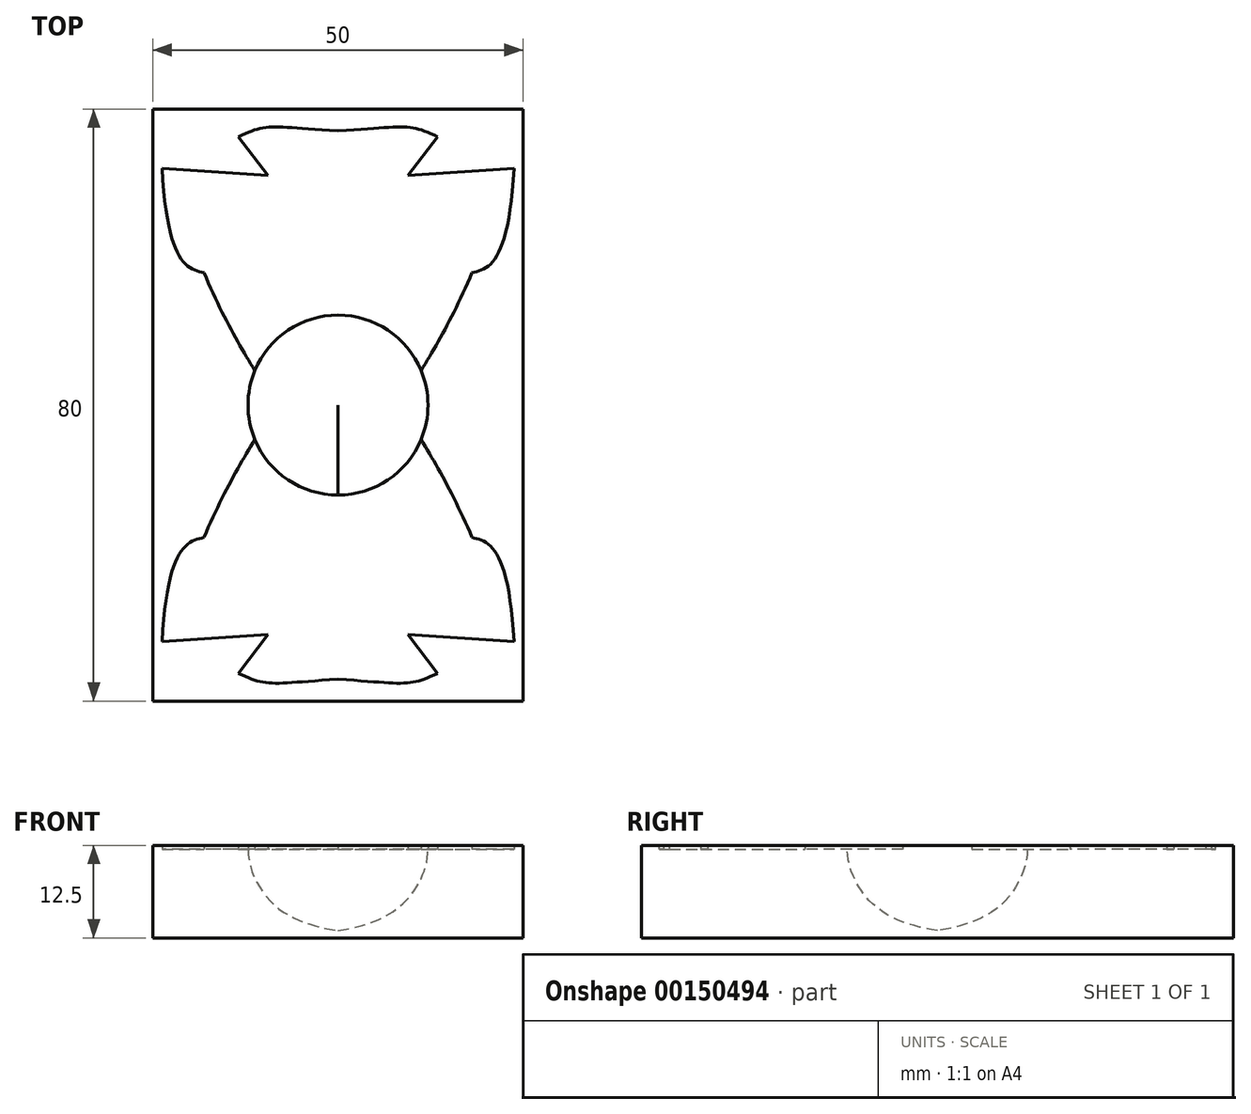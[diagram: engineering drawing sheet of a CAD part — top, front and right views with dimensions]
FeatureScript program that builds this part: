
annotation { "Feature Type Name" : "Feature", "Feature Type Description" : "" }
export const myFeature = defineFeature(function(context is Context, id is Id, definition is map)
    precondition{}
    {
        {
            var Q0;
            Q0=qCreatedBy(makeId("Top.planeOp"),FACE);
            var sketch = newSketch(context, id + "F0", { "sketchPlane" : qUnion([Q0])});
            skLineSegment(sketch, "E0.bottom", {"start": v(-60.64, -67.64) * mm, "end": v(-10.64, -67.64) * mm});
            skLineSegment(sketch, "E0.top", {"start": v(-60.64, -147.64) * mm, "end": v(-10.64, -147.64) * mm});
            skLineSegment(sketch, "E0.left", {"start": v(-60.64, -67.64) * mm, "end": v(-60.64, -147.64) * mm});
            skLineSegment(sketch, "E0.right", {"start": v(-10.64, -67.64) * mm, "end": v(-10.64, -147.64) * mm});
            skSolve(sketch);
        }
        {
            var Q0;
            Q0=makeQuery(id+"F0.imprint","IMPRINT",FACE,{"disambiguationData":[TD([[makeQuery(id+"F0.imprint","IMPRINT",EDGE,{"derivedFrom":sQuery(id+"F0.wireOp",EDGE,"E0.bottom")}),-1.0]])]});
            extrude(context, id + "F1", {"entities" : qUnion([Q0]), "depth" : 12 * mm});
        }
        {
            var Q0;
            Q0=makeQuery(id+"F1.opExtrude","SWEPT_FACE",FACE,{"disambiguationData":[OSD([sQuery(id+"F0.wireOp",EDGE,"E0.right")])]});
            cPlane(context, id + "F2", {"entities" : qUnion([Q0]), "cplaneType" : CPlaneType.OFFSET, "offset" : 25 * mm, "oppositeDirection" : true, "width" : 150 * mm, "height" : 150 * mm});
        }
        {
            var Q0;
            Q0=qCreatedBy(id+"F2.planeOp",FACE);
            var sketch = newSketch(context, id + "F3", { "sketchPlane" : qUnion([Q0])});
            skFitSpline(sketch, "E1", {"points": [v(-107.63, 0.98) * mm, v(-116.16, 4.39) * mm, v(-119.8, 11.95) * mm, v(-116.72, 18.21) * mm, v(-107.63, 21) * mm], "startDerivative": vector(-36.59, 5.94) * mm, "endDerivative": vector(38.78, 5.13) * mm});
            skArc(sketch, "E2.trimOffspring", {"start": v(-107.64, 0.98) * mm, "mid": v(-107.64, 0.98) * mm, "end": v(-107.63, 0.98) * mm});
            skLineSegment(sketch, "E3", {"start": v(-107.64, 28.47) * mm, "end": v(-107.64, -7.44) * mm});
            skSolve(sketch);
        }
        {
            var Q0;
            {var subQ0=sQuery(id+"F3.wireOp",EDGE,"E1");Q0=makeQuery(id+"F3.imprint","IMPRINT",FACE,{"disambiguationData":[TD([[makeQuery(id+"F3.imprint","IMPRINT",EDGE,{"derivedFrom":subQ0}),-1.0]])]});}
            var Q1;
            Q1=sQuery(id+"F3.wireOp",EDGE,"E3");
            revolve(context, id + "F4", {"operationType" : NewBodyOperationType.REMOVE, "entities" : qUnion([Q0]), "axis" : qUnion([Q1]), "revolveType" : RevolveType.FULL, "oppositeDirection" : true});
        }
        {
            var Q0;
            Q0=makeQuery(id+"F1.opExtrude","CAP_FACE",FACE,{"disambiguationData":[OSD([sQuery(id+"F0.wireOp",EDGE,"E0.bottom"),sQuery(id+"F0.wireOp",EDGE,"E0.top"),sQuery(id+"F0.wireOp",EDGE,"E0.left"),sQuery(id+"F0.wireOp",EDGE,"E0.right")])],"isStart":false});
            var sketch = newSketch(context, id + "F5", { "sketchPlane" : qUnion([Q0])});
            skPoint(sketch, "E4.3.internal.snap0", {"position": v(-24.7, -91.33) * mm});
            skLineSegment(sketch, "E5.MirrorCS", {"start": v(-49.1, -71.4) * mm, "end": v(-45.08, -76.62) * mm});
            skLineSegment(sketch, "E6.MirrorCS", {"start": v(-45.08, -76.62) * mm, "end": v(-59.42, -75.67) * mm});
            skFitSpline(sketch, "E7.MirrorCS", {"points": [v(-35.64, -70.6) * mm, v(-49.1, -71.4) * mm], "startDerivative": vector(-27, 1.87) * mm, "endDerivative": vector(-11.52, -5.64) * mm});
            skFitSpline(sketch, "E8", {"points": [v(-59.42, -75.67) * mm, v(-53.45, -89.8) * mm, v(-48.56, -91.27) * mm, v(-40.85, -98.96) * mm, v(-58.03, -137.94) * mm], "startDerivative": vector(9.18, -160) * mm, "endDerivative": vector(-51.19, -186.4) * mm});
            skPoint(sketch, "E9.end.orphan", {"position": v(-10.64, -89.12) * mm});
            skLineSegment(sketch, "E10.bottom", {"start": v(-60.64, -67.64) * mm, "end": v(-10.64, -67.64) * mm});
            skLineSegment(sketch, "E10.top", {"start": v(-60.64, -147.64) * mm, "end": v(-10.64, -147.64) * mm});
            skLineSegment(sketch, "E10.left", {"start": v(-60.64, -67.64) * mm, "end": v(-60.64, -147.64) * mm});
            skLineSegment(sketch, "E10.right", {"start": v(-10.64, -67.64) * mm, "end": v(-10.64, -147.64) * mm});
            skLineSegment(sketch, "E11", {"start": v(-35.64, -107.64) * mm, "end": v(-47.8, -107.64) * mm});
            skLineSegment(sketch, "E12", {"start": v(-35.64, -107.64) * mm, "end": v(-35.64, -95.47) * mm});
            skPoint(sketch, "E4.0.internal.orphan", {"position": v(-12.1, -75.88) * mm});
            skPoint(sketch, "E4.2.internal.orphan", {"position": v(-24.7, -91.49) * mm});
            skPoint(sketch, "E4.4.internal.orphan", {"position": v(-12.1, -137.5) * mm});
            skFitSpline(sketch, "E13.MirrorCS", {"points": [v(-35.64, -70.6) * mm, v(-22.17, -71.4) * mm], "startDerivative": vector(27, 1.87) * mm, "endDerivative": vector(11.52, -5.64) * mm});
            skLineSegment(sketch, "E14.MirrorCS", {"start": v(-22.17, -71.4) * mm, "end": v(-26.2, -76.62) * mm});
            skLineSegment(sketch, "E15.MirrorCS", {"start": v(-26.2, -76.62) * mm, "end": v(-11.86, -75.67) * mm});
            skFitSpline(sketch, "E16.MirrorCS", {"points": [v(-11.86, -75.67) * mm, v(-17.83, -89.8) * mm, v(-22.72, -91.27) * mm, v(-30.43, -98.96) * mm, v(-13.25, -137.94) * mm], "startDerivative": vector(-9.18, -160) * mm, "endDerivative": vector(51.19, -186.4) * mm});
            skPoint(sketch, "E17.orphan", {"position": v(-42.15, -97.36) * mm});
            skPoint(sketch, "E18.MirrorCS.end.orphan", {"position": v(-29.13, -97.36) * mm});
            skPoint(sketch, "E18.MirrorCS.start.orphan", {"position": v(-29.63, -97.06) * mm});
            skCircle(sketch, "E19", {"center": v(-35.64, -107.64) * mm, "radius": 12.16 * mm});
            skFitSpline(sketch, "E20.MirrorCS", {"points": [v(-59.42, -139.6) * mm, v(-53.45, -125.47) * mm, v(-48.56, -124) * mm, v(-40.85, -116.31) * mm, v(-58.03, -77.33) * mm], "startDerivative": vector(9.18, 160) * mm, "endDerivative": vector(-51.19, 186.4) * mm});
            skLineSegment(sketch, "E21.MirrorCS", {"start": v(-45.08, -138.65) * mm, "end": v(-59.42, -139.6) * mm});
            skLineSegment(sketch, "E22.MirrorCS", {"start": v(-49.1, -143.88) * mm, "end": v(-45.08, -138.65) * mm});
            skFitSpline(sketch, "E23.MirrorCS", {"points": [v(-35.64, -144.67) * mm, v(-49.1, -143.88) * mm], "startDerivative": vector(-27, -1.87) * mm, "endDerivative": vector(-11.52, 5.64) * mm});
            skFitSpline(sketch, "E24.MirrorCS", {"points": [v(-35.64, -144.67) * mm, v(-22.17, -143.88) * mm], "startDerivative": vector(27, -1.87) * mm, "endDerivative": vector(11.52, 5.64) * mm});
            skLineSegment(sketch, "E25.MirrorCS", {"start": v(-22.17, -143.88) * mm, "end": v(-26.2, -138.65) * mm});
            skLineSegment(sketch, "E26.MirrorCS", {"start": v(-26.2, -138.65) * mm, "end": v(-11.86, -139.6) * mm});
            skFitSpline(sketch, "E27.MirrorCS", {"points": [v(-11.86, -139.6) * mm, v(-17.83, -125.47) * mm, v(-22.72, -124) * mm, v(-30.43, -116.31) * mm, v(-13.25, -77.33) * mm], "startDerivative": vector(-9.18, 160) * mm, "endDerivative": vector(51.19, 186.4) * mm});
            skSolve(sketch);
        }
        {
            var Q0;
            Q0=makeQuery(id+"F5.imprint","IMPRINT",FACE,{"disambiguationData":[TD([[makeQuery(id+"F5.imprint","IMPRINT",EDGE,{"derivedFrom":sQuery(id+"F5.wireOp",EDGE,"E5.MirrorCS")}),-1.0]])]});
            extrude(context, id + "F6", {"entities" : qUnion([Q0]), "operationType" : NewBodyOperationType.ADD, "depth" : 0.5 * mm});
        }
    });
